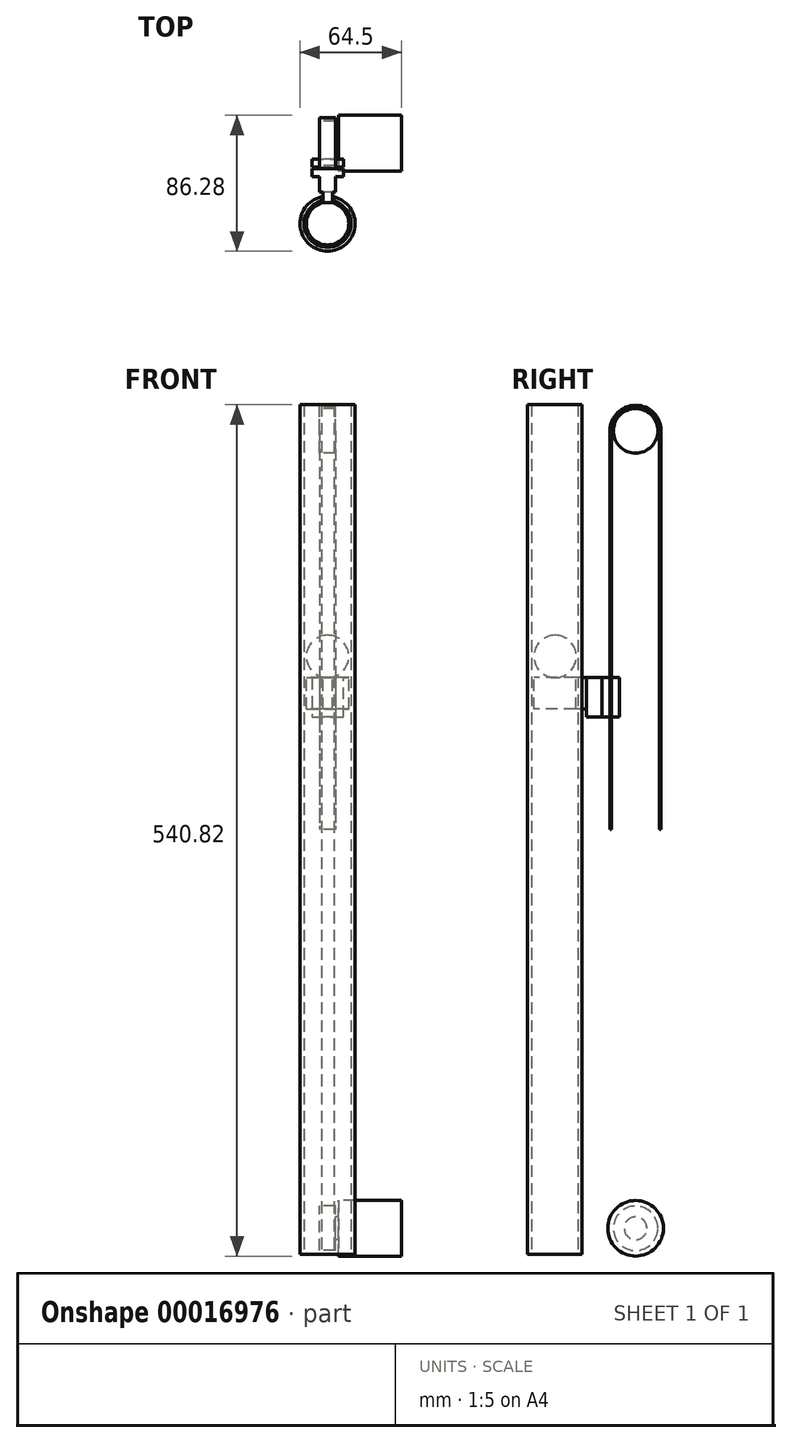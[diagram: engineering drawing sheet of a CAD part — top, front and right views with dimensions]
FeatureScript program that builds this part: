
annotation { "Feature Type Name" : "Feature", "Feature Type Description" : "" }
export const myFeature = defineFeature(function(context is Context, id is Id, definition is map)
    precondition{}
    {
        {
            var Q0;
            Q0=qCreatedBy(makeId("Right.planeOp"),FACE);
            var sketch = newSketch(context, id + "F0", { "sketchPlane" : qUnion([Q0])});
            skArc(sketch, "E0", {"start": v(-83.84, 96.48) * mm, "mid": v(-70.35, 109.97) * mm, "end": v(-83.84, 123.47) * mm});
            skLineSegment(sketch, "E1", {"start": v(-83.84, 123.47) * mm, "end": v(-83.84, 82.4) * mm});
            skSolve(sketch);
        }
        {
            var Q0;
            {var subQ1=sQuery(id+"F0.wireOp",EDGE,"E0");Q0=makeQuery(id+"F0.imprint","IMPRINT",FACE,{"disambiguationData":[TD([[makeQuery(id+"F0.imprint","IMPRINT",EDGE,{"derivedFrom":subQ1}),1.0]])]});}
            var Q1;
            Q1=sQuery(id+"F0.wireOp",EDGE,"E1");
            revolve(context, id + "F1", {"entities" : qUnion([Q0]), "axis" : qUnion([Q1]), "revolveType" : RevolveType.FULL});
        }
        {
            var Q0;
            Q0=qCreatedBy(makeId("Top.planeOp"),FACE);
            var sketch = newSketch(context, id + "F2", { "sketchPlane" : qUnion([Q0])});
            skArc(sketch, "E2", {"start": v(-4, -69.39) * mm, "mid": v(0, -98.84) * mm, "end": v(4, -69.39) * mm});
            skArc(sketch, "E3", {"start": v(-4, -66.8) * mm, "mid": v(0, -101.34) * mm, "end": v(4, -66.8) * mm});
            skLineSegment(sketch, "E4.left", {"start": v(-4, -66.8) * mm, "end": v(-4, -69.39) * mm});
            skLineSegment(sketch, "E4.right", {"start": v(4, -66.8) * mm, "end": v(4, -69.39) * mm});
            skSolve(sketch);
        }
        {
            var Q0;
            Q0=makeQuery(id+"F2.imprint","IMPRINT",FACE,{"disambiguationData":[TD([[makeQuery(id+"F2.imprint","IMPRINT",EDGE,{"derivedFrom":sQuery(id+"F2.wireOp",EDGE,"E2")}),-1.0]])]});
            extrude(context, id + "F3", {"entities" : qUnion([Q0]), "depth" : (26.99 * 10) * mm, "hasSecondDirection" : true, "secondDirectionOppositeDirection" : true, "secondDirectionDepth" : (26.99 * 10) * mm});
        }
        {
            var Q0;
            Q0=qCreatedBy(makeId("Right.planeOp"),FACE);
            var sketch = newSketch(context, id + "F4", { "sketchPlane" : qUnion([Q0])});
            skLineSegment(sketch, "E5.bottom", {"start": v(-63.86, 96.48) * mm, "end": v(-48.86, 96.48) * mm});
            skLineSegment(sketch, "E5.top", {"start": v(-63.86, 71.4) * mm, "end": v(-48.86, 71.4) * mm});
            skLineSegment(sketch, "E5.left", {"start": v(-63.86, 96.48) * mm, "end": v(-63.86, 71.4) * mm});
            skLineSegment(sketch, "E5.right", {"start": v(-48.86, 96.48) * mm, "end": v(-48.86, 71.4) * mm});
            skCircle(sketch, "E6", {"center": v(-83.84, 109.97) * mm, "radius": 13.5 * mm});
            skSolve(sketch);
        }
        {
            var Q0;
            Q0=makeQuery(id+"F4.imprint","IMPRINT",FACE,{"disambiguationData":[TD([[makeQuery(id+"F4.imprint","IMPRINT",EDGE,{"derivedFrom":sQuery(id+"F4.wireOp",EDGE,"E5.bottom")}),-1.0]])]});
            extrude(context, id + "F5", {"entities" : qUnion([Q0]), "depth" : 5 * mm, "hasSecondDirection" : true, "secondDirectionOppositeDirection" : true, "secondDirectionDepth" : 5 * mm});
        }
        {
            var Q0;
            Q0=makeQuery(id+"F5.opExtrude","SWEPT_FACE",FACE,{"disambiguationData":[OSD([sQuery(id+"F4.wireOp",EDGE,"E5.bottom")])]});
            var sketch = newSketch(context, id + "F6", { "sketchPlane" : qUnion([Q0])});
            skCircle(sketch, "E7", {"center": v(0, -83.84) * mm, "radius": 13.5 * mm});
            skLineSegment(sketch, "E8.bottom", {"start": v(-3, -62.67) * mm, "end": v(3, -62.67) * mm});
            skLineSegment(sketch, "E8.top", {"start": v(-3, -72.15) * mm, "end": v(3, -72.15) * mm});
            skLineSegment(sketch, "E8.left", {"start": v(-3, -62.67) * mm, "end": v(-3, -72.15) * mm});
            skLineSegment(sketch, "E8.right", {"start": v(3, -62.67) * mm, "end": v(3, -72.15) * mm});
            skSolve(sketch);
        }
        {
            var Q0;
            Q0=makeQuery(id+"F6.imprint","IMPRINT",FACE,{"disambiguationData":[TD([[makeQuery(id+"F6.imprint","IMPRINT",EDGE,{"derivedFrom":sQuery(id+"F6.wireOp",EDGE,"E7")}),1.0]])]});
            var Q1;
            {var subQ3=sQuery(id+"F6.wireOp",EDGE,"E8.left");var subQ5=sQuery(id+"F6.wireOp",EDGE,"E7");var subQ7=makeQuery(id+"F6.imprint","INTERSECT",VERTEX,{"derivedFrom":[subQ5,subQ3]});Q1=makeQuery(id+"F6.imprint","IMPRINT",FACE,{"disambiguationData":[TD([[makeQuery(id+"F6.imprint","IMPRINT",EDGE,{"disambiguationData":[TD([[subQ7,1.0]])],"derivedFrom":subQ5}),-1.0]])]});}
            extrude(context, id + "F7", {"entities" : qUnion([Q0, Q1]), "operationType" : NewBodyOperationType.ADD, "oppositeDirection" : true, "depth" : 20 * mm});
        }
        {
            var Q0;
            Q0=qCreatedBy(makeId("Right.planeOp"),FACE);
            var sketch = newSketch(context, id + "F8", { "sketchPlane" : qUnion([Q0])});
            skCircle(sketch, "E9", {"center": v(-32.72, 253.27) * mm, "radius": 14.13 * mm});
            skCircle(sketch, "E10", {"center": v(-32.72, -253.27) * mm, "radius": 14.13 * mm});
            skSolve(sketch);
        }
        {
            var Q0;
            Q0=makeQuery(id+"F8.imprint","IMPRINT",FACE,{"disambiguationData":[TD([[makeQuery(id+"F8.imprint","IMPRINT",EDGE,{"derivedFrom":sQuery(id+"F8.wireOp",EDGE,"E9")}),1.0]])]});
            var Q1;
            Q1=makeQuery(id+"F8.imprint","IMPRINT",FACE,{"disambiguationData":[TD([[makeQuery(id+"F8.imprint","IMPRINT",EDGE,{"derivedFrom":sQuery(id+"F8.wireOp",EDGE,"E10")}),1.0]])]});
            extrude(context, id + "F9", {"entities" : qUnion([Q0, Q1]), "depth" : 5 * mm, "hasSecondDirection" : true, "secondDirectionOppositeDirection" : true, "secondDirectionDepth" : 5 * mm});
        }
        {
            var Q0;
            Q0=qCreatedBy(makeId("Right.planeOp"),FACE);
            var sketch = newSketch(context, id + "F10", { "sketchPlane" : qUnion([Q0])});
            skCircle(sketch, "E11.0.0", {"center": v(-32.72, 253.27) * mm, "radius": 14.13 * mm});
            skArc(sketch, "E12", {"start": v(-17.48, 253.27) * mm, "mid": v(-32.72, 268.51) * mm, "end": v(-47.97, 253.27) * mm});
            skLineSegment(sketch, "E13", {"start": v(-47.97, 253.27) * mm, "end": v(-47.97, 0) * mm});
            skLineSegment(sketch, "E14", {"start": v(-17.48, 253.27) * mm, "end": v(-17.48, 0) * mm});
            skLineSegment(sketch, "E15", {"start": v(-48.97, 253.28) * mm, "end": v(-48.97, 0) * mm});
            skArc(sketch, "E16", {"start": v(-16.48, 253.28) * mm, "mid": v(-32.72, 269.52) * mm, "end": v(-48.97, 253.28) * mm});
            skLineSegment(sketch, "E17", {"start": v(-16.48, 253.28) * mm, "end": v(-16.48, 0) * mm});
            skLineSegment(sketch, "E18", {"start": v(-48.97, 0) * mm, "end": v(-16.48, 0) * mm});
            skArc(sketch, "E19.MirrorCS", {"start": v(-16.48, -253.28) * mm, "mid": v(-32.72, -269.52) * mm, "end": v(-48.97, -253.28) * mm});
            skCircle(sketch, "E20.MirrorC", {"center": v(-32.72, -253.27) * mm, "radius": 14.13 * mm});
            skArc(sketch, "E21.MirrorCS", {"start": v(-17.48, -253.27) * mm, "mid": v(-32.72, -268.51) * mm, "end": v(-47.97, -253.27) * mm});
            skLineSegment(sketch, "E22.MirrorCS", {"start": v(-47.97, -253.27) * mm, "end": v(-47.97, 0) * mm});
            skLineSegment(sketch, "E23.MirrorCS", {"start": v(-17.48, -253.27) * mm, "end": v(-17.48, 0) * mm});
            skLineSegment(sketch, "E24.MirrorCS", {"start": v(-48.97, -253.28) * mm, "end": v(-48.97, 0) * mm});
            skLineSegment(sketch, "E25.MirrorCS", {"start": v(-16.48, -253.28) * mm, "end": v(-16.48, 0) * mm});
            skSolve(sketch);
        }
        {
            var Q0;
            Q0=makeQuery(id+"F10.imprint","IMPRINT",FACE,{"disambiguationData":[TD([[makeQuery(id+"F10.imprint","IMPRINT",EDGE,{"derivedFrom":sQuery(id+"F10.wireOp",EDGE,"E12")}),-1.0]])]});
            var Q1;
            Q1=makeQuery(id+"F10.imprint","IMPRINT",FACE,{"disambiguationData":[TD([[makeQuery(id+"F10.imprint","IMPRINT",EDGE,{"derivedFrom":sQuery(id+"F10.wireOp",EDGE,"E19.MirrorCS")}),-1.0]])]});
            extrude(context, id + "F11", {"entities" : qUnion([Q0, Q1]), "depth" : 5 * mm, "hasSecondDirection" : true, "secondDirectionOppositeDirection" : true, "secondDirectionDepth" : 5 * mm});
        }
        {
            var Q0;
            Q0=makeQuery(id+"F11.opExtrude","SWEPT_FACE",FACE,{"disambiguationData":[OSD([sQuery(id+"F10.wireOp",EDGE,"E13"),sQuery(id+"F10.wireOp",EDGE,"E22.MirrorCS")])]});
            var sketch = newSketch(context, id + "F12", { "sketchPlane" : qUnion([Q0])});
            skLineSegment(sketch, "E26.0.0", {"start": v(10, 96.48) * mm, "end": v(10, 71.4) * mm});
            skLineSegment(sketch, "E26.0.1", {"start": v(10, 71.4) * mm, "end": v(-10, 71.4) * mm});
            skLineSegment(sketch, "E26.0.2", {"start": v(-10, 71.4) * mm, "end": v(-10, 96.48) * mm});
            skLineSegment(sketch, "E26.0.3", {"start": v(-10, 96.48) * mm, "end": v(10, 96.48) * mm});
            skSolve(sketch);
        }
        {
            var Q0;
            {var subQ5=sQuery(id+"F12.wireOp",EDGE,"E26.0.0");Q0=makeQuery(id+"F12.imprint","IMPRINT",FACE,{"disambiguationData":[TD([[makeQuery(id+"F12.imprint","IMPRINT",EDGE,{"derivedFrom":subQ5}),-1.0]])]});}
            var Q1;
            {var subQ0=sQuery(id+"F10.wireOp",EDGE,"E13");var subQ1=sQuery(id+"F10.wireOp",EDGE,"E22.MirrorCS");var subQ5=sQuery(id+"F12.wireOp",EDGE,"E26.0.1");var subQ7=makeQuery(id+"F11.opExtrude","CAP_EDGE",EDGE,{"disambiguationData":[OSD([subQ0,subQ1])],"isStart":true});var subQ9=makeQuery(id+"F12.imprint","INTERSECT",VERTEX,{"derivedFrom":[subQ7,subQ5]});Q1=makeQuery(id+"F12.imprint","IMPRINT",FACE,{"disambiguationData":[TD([[makeQuery(id+"F12.imprint","IMPRINT",EDGE,{"disambiguationData":[TD([[subQ9,-1.0]])],"derivedFrom":subQ5}),-1.0]])]});}
            var Q2;
            {var subQ5=sQuery(id+"F12.wireOp",EDGE,"E26.0.2");Q2=makeQuery(id+"F12.imprint","IMPRINT",FACE,{"disambiguationData":[TD([[makeQuery(id+"F12.imprint","IMPRINT",EDGE,{"derivedFrom":subQ5}),-1.0]])]});}
            extrude(context, id + "F13", {"entities" : qUnion([Q0, Q1, Q2]), "operationType" : NewBodyOperationType.ADD, "depth" : 5 * mm});
        }
        {
            var Q0;
            Q0=makeQuery(id+"F11.opExtrude","SWEPT_FACE",FACE,{"disambiguationData":[OSD([sQuery(id+"F10.wireOp",EDGE,"E15"),sQuery(id+"F10.wireOp",EDGE,"E24.MirrorCS")])]});
            var sketch = newSketch(context, id + "F14", { "sketchPlane" : qUnion([Q0])});
            skLineSegment(sketch, "E27.0.0", {"start": v(-10, 96.48) * mm, "end": v(-10, 71.4) * mm});
            skLineSegment(sketch, "E27.0.1", {"start": v(-10, 71.4) * mm, "end": v(10, 71.4) * mm});
            skLineSegment(sketch, "E27.0.2", {"start": v(10, 71.4) * mm, "end": v(10, 96.48) * mm});
            skLineSegment(sketch, "E27.0.3", {"start": v(10, 96.48) * mm, "end": v(-10, 96.48) * mm});
            skSolve(sketch);
        }
        {
            var Q0;
            {var subQ5=sQuery(id+"F14.wireOp",EDGE,"E27.0.2");Q0=makeQuery(id+"F14.imprint","IMPRINT",FACE,{"disambiguationData":[TD([[makeQuery(id+"F14.imprint","IMPRINT",EDGE,{"derivedFrom":subQ5}),1.0]])]});}
            var Q1;
            {var subQ5=sQuery(id+"F14.wireOp",EDGE,"E27.0.0");Q1=makeQuery(id+"F14.imprint","IMPRINT",FACE,{"disambiguationData":[TD([[makeQuery(id+"F14.imprint","IMPRINT",EDGE,{"derivedFrom":subQ5}),1.0]])]});}
            extrude(context, id + "F15", {"entities" : qUnion([Q0, Q1]), "operationType" : NewBodyOperationType.ADD, "depth" : 5 * mm});
        }
        {
            var Q0;
            Q0=makeQuery(id+"F9.opExtrude","CAP_FACE",FACE,{"disambiguationData":[OSD([sQuery(id+"F8.wireOp",EDGE,"E10")])],"isStart":false});
            var sketch = newSketch(context, id + "F16", { "sketchPlane" : qUnion([Q0])});
            skCircle(sketch, "E28.0.0", {"center": v(-32.72, -253.27) * mm, "radius": 14.13 * mm});
            skCircle(sketch, "E29", {"center": v(-32.72, -253.27) * mm, "radius": 7.21 * mm});
            skSolve(sketch);
        }
        {
            var Q0;
            Q0=makeQuery(id+"F16.imprint","IMPRINT",FACE,{"disambiguationData":[TD([[makeQuery(id+"F16.imprint","IMPRINT",EDGE,{"derivedFrom":sQuery(id+"F16.wireOp",EDGE,"E29")}),1.0]])]});
            extrude(context, id + "F17", {"entities" : qUnion([Q0]), "depth" : 2 * mm});
        }
        {
            var Q0;
            Q0=makeQuery(id+"F17.opExtrude","CAP_FACE",FACE,{"disambiguationData":[OSD([sQuery(id+"F16.wireOp",EDGE,"E29")])],"isStart":false});
            var sketch = newSketch(context, id + "F18", { "sketchPlane" : qUnion([Q0])});
            skCircle(sketch, "E30.0.0", {"center": v(-32.72, -253.27) * mm, "radius": 7.21 * mm});
            skCircle(sketch, "E31", {"center": v(-32.72, -253.27) * mm, "radius": 17.67 * mm});
            skSolve(sketch);
        }
        {
            var Q0;
            Q0=makeQuery(id+"F18.imprint","IMPRINT",FACE,{"disambiguationData":[TD([[makeQuery(id+"F18.imprint","IMPRINT",EDGE,{"derivedFrom":sQuery(id+"F18.wireOp",EDGE,"E30.0.0")}),-1.0]])]});
            var Q1;
            Q1=makeQuery(id+"F18.imprint","IMPRINT",FACE,{"disambiguationData":[TD([[makeQuery(id+"F18.imprint","IMPRINT",EDGE,{"derivedFrom":sQuery(id+"F18.wireOp",EDGE,"E30.0.0")}),1.0]])]});
            extrude(context, id + "F19", {"entities" : qUnion([Q0, Q1]), "operationType" : NewBodyOperationType.ADD, "depth" : 40 * mm});
        }
    });
